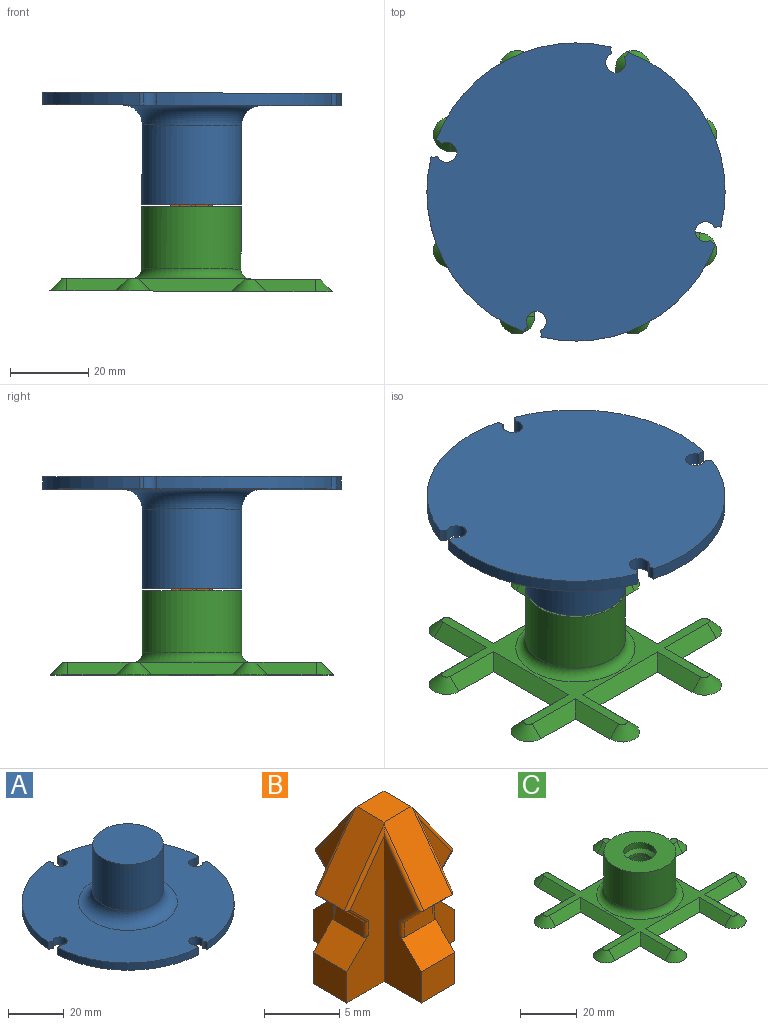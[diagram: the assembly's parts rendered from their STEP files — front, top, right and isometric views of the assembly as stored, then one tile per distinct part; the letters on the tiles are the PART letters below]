
ASSEMBLY  parts=3 mates=1
PART A: 29 faces, bbox 76.1x76.1x28.6 mm
  f0: cylinder r=12.7mm len=25.4mm, axis (0,0,1), area 1621.5mm2, adj f1,f28
  f1: plane 25.4x25.4mm, normal (0,0,1), area 506.7mm2, adj f0
  f2: cylinder r=2.29mm len=3.18mm, axis (0,0,1), area 5.4mm2, adj f3,f25,f26,f27
  f3: cylinder r=38.1mm len=35.75mm, axis (0,0,1), area 175.5mm2, adj f2,f4,f26,f27
  f4: cylinder r=2.29mm len=3.18mm, axis (0,0,1), area 5.4mm2, adj f3,f5,f26,f27
  f5: cylinder r=0.03mm len=3.18mm, axis (0,0,1), area 0.1mm2, adj f4,f6,f26,f27
  f6: cylinder r=2.54mm len=5.08mm, axis (0,0,1), area 39.4mm2, adj f5,f7,f26,f27
  f7: cylinder r=0.03mm len=3.18mm, axis (0,0,1), area 0.1mm2, adj f6,f8,f26,f27
  f8: cylinder r=2.29mm len=3.18mm, axis (0,0,1), area 5.4mm2, adj f7,f9,f26,f27
  f9: cylinder r=38.1mm len=35.75mm, axis (0,0,1), area 175.5mm2, adj f8,f10,f26,f27
  f10: cylinder r=2.29mm len=3.18mm, axis (0,0,1), area 5.4mm2, adj f9,f11,f26,f27
  f11: cylinder r=0.03mm len=3.18mm, axis (0,0,1), area 0.1mm2, adj f10,f12,f26,f27
  f12: cylinder r=2.54mm len=5.08mm, axis (0,0,1), area 39.4mm2, adj f11,f13,f26,f27
  f13: cylinder r=0.03mm len=3.18mm, axis (0,0,1), area 0.1mm2, adj f12,f14,f26,f27
  f14: cylinder r=2.29mm len=3.18mm, axis (0,0,1), area 5.4mm2, adj f13,f15,f26,f27
  f15: cylinder r=38.1mm len=35.75mm, axis (0,0,1), area 175.5mm2, adj f14,f16,f26,f27
  f16: cylinder r=2.29mm len=3.18mm, axis (0,0,1), area 5.4mm2, adj f15,f17,f26,f27
  f17: cylinder r=0.03mm len=3.18mm, axis (0,0,1), area 0.1mm2, adj f16,f18,f26,f27
  f18: cylinder r=2.54mm len=5.08mm, axis (0,0,1), area 39.4mm2, adj f17,f19,f26,f27
  f19: cylinder r=0.03mm len=3.18mm, axis (0,0,1), area 0.1mm2, adj f18,f20,f26,f27
  f20: cylinder r=2.29mm len=3.18mm, axis (0,0,1), area 5.4mm2, adj f19,f21,f26,f27
  f21: cylinder r=38.1mm len=35.75mm, axis (0,0,1), area 175.5mm2, adj f20,f22,f26,f27
  f22: cylinder r=2.29mm len=3.18mm, axis (0,0,1), area 5.4mm2, adj f21,f23,f26,f27
  f23: cylinder r=0.03mm len=3.18mm, axis (0,0,1), area 0.1mm2, adj f22,f24,f26,f27
  f24: cylinder r=2.54mm len=5.08mm, axis (0,0,1), area 39.4mm2, adj f23,f25,f26,f27
  f25: cylinder r=0.03mm len=3.18mm, axis (0,0,1), area 0.1mm2, adj f2,f24,f26,f27
  f26: plane 76.06x76.06mm, normal (0,0,1), area 3464.8mm2, adj f2,f3,f4,f5,f6,f7,f8,f9
  f27: plane 76.06x76.06mm, normal (0,0,-1), area 4458mm2, adj f2,f3,f4,f5,f6,f7,f8,f9
  f28: torus R=17.78mm, axis (0,0,1), area 729.3mm2, adj f0,f26
PART B: 54 faces, bbox 10.2x10.2x12.7 mm
  f0: plane 11.82x3.49mm, normal (1,0,0), area 26.4mm2, adj f5,f14,f15,f29,f45,f46,f47
  f1: plane 11.82x3.49mm, normal (-1,0,0), area 26.4mm2, adj f13,f14,f15,f29,f51,f52,f53
  f2: plane 5.3x3.81mm, normal (-0.81,0,0.58), area 17.4mm2, adj f4,f20,f22,f26,f38,f50
  f3: plane 5.3x3.81mm, normal (0.81,0,0.58), area 17.4mm2, adj f4,f16,f22,f26,f32,f44
  f4: plane 2.54x2.54mm, normal (0,0,1), area 6.5mm2, adj f2,f3,f22,f26
  f5: plane 11.82x3.49mm, normal (0,-1,0), area 26.4mm2, adj f0,f7,f15,f18,f42,f43,f44
  f6: plane 11.82x3.49mm, normal (0,1,0), area 26.4mm2, adj f7,f8,f15,f18,f30,f31,f32
  f7: plane 3.18x2.54mm, normal (1,0,0), area 8.1mm2, adj f5,f6,f15,f18
  f8: plane 11.82x3.49mm, normal (1,0,0), area 26.4mm2, adj f6,f9,f15,f25,f33,f34,f35
  f9: plane 3.18x2.54mm, normal (0,1,0), area 8.1mm2, adj f8,f10,f15,f25
  f10: plane 11.82x3.49mm, normal (-1,0,0), area 26.4mm2, adj f9,f11,f15,f25,f39,f40,f41
  f11: plane 11.82x3.49mm, normal (0,1,0), area 26.4mm2, adj f10,f12,f15,f21,f36,f37,f38
  f12: plane 3.18x2.54mm, normal (-1,0,0), area 8.1mm2, adj f11,f13,f15,f21
  f13: plane 11.82x3.49mm, normal (0,-1,0), area 26.4mm2, adj f1,f12,f15,f21,f48,f49,f50
  f14: plane 3.18x2.54mm, normal (0,-1,0), area 8.1mm2, adj f0,f1,f15,f29
  f15: plane 10.16x10.16mm, normal (0,0,-1), area 54.4mm2, adj f0,f1,f5,f6,f7,f8,f9,f10
  f16: plane 2.67x1.8mm, normal (0.71,0,-0.71), area 6.8mm2, adj f3,f17,f31,f43
  f17: plane 2.67x1.27mm, normal (1,0,0), area 3.4mm2, adj f16,f18,f30,f42
  f18: plane 3.18x2.05mm, normal (0.71,0,0.71), area 8.1mm2, adj f5,f6,f7,f17,f30,f42
  f19: plane 2.67x1.27mm, normal (-1,0,0), area 3.4mm2, adj f20,f21,f36,f48
  f20: plane 2.67x1.8mm, normal (-0.71,0,-0.71), area 6.8mm2, adj f2,f19,f37,f49
  f21: plane 3.18x2.05mm, normal (-0.71,0,0.71), area 8.1mm2, adj f11,f12,f13,f19,f36,f48
  f22: plane 5.3x3.81mm, normal (0,-0.81,0.58), area 17.4mm2, adj f2,f3,f4,f28,f46,f52
  f23: plane 2.67x1.8mm, normal (0,0.71,-0.71), area 6.8mm2, adj f24,f26,f34,f40
  f24: plane 2.67x1.27mm, normal (0,1,0), area 3.4mm2, adj f23,f25,f35,f41
  f25: plane 3.18x2.05mm, normal (0,0.71,0.71), area 8.1mm2, adj f8,f9,f10,f24,f35,f41
  f26: plane 5.3x3.81mm, normal (0,0.81,0.58), area 17.4mm2, adj f2,f3,f4,f23,f33,f39
  f27: plane 2.67x1.27mm, normal (0,-1,0), area 3.4mm2, adj f28,f29,f45,f51
  f28: plane 2.67x1.8mm, normal (0,-0.71,-0.71), area 6.8mm2, adj f22,f27,f47,f53
  f29: plane 3.18x2.05mm, normal (0,-0.71,0.71), area 8.1mm2, adj f0,f1,f14,f27,f45,f51
  f30: cylinder r=0.25mm len=1.38mm, axis (0,0,-1), area 0.5mm2, adj f6,f17,f18,f31
  f31: cylinder r=0.25mm len=2.05mm, axis (-0.71,0,-0.71), area 1mm2, adj f6,f16,f30,f32
  f32: cylinder r=0.25mm len=5.36mm, axis (0.58,0,-0.81), area 2.4mm2, adj f3,f6,f31,f33
  f33: cylinder r=0.25mm len=5.36mm, axis (0,0.58,-0.81), area 2.4mm2, adj f8,f26,f32,f34
  f34: cylinder r=0.25mm len=2.05mm, axis (0,-0.71,-0.71), area 1mm2, adj f8,f23,f33,f35
  f35: cylinder r=0.25mm len=1.38mm, axis (0,0,-1), area 0.5mm2, adj f8,f24,f25,f34
  f36: cylinder r=0.25mm len=1.38mm, axis (0,0,1), area 0.5mm2, adj f11,f19,f21,f37
  f37: cylinder r=0.25mm len=2.05mm, axis (-0.71,0,0.71), area 1mm2, adj f11,f20,f36,f38
  f38: cylinder r=0.25mm len=5.36mm, axis (0.58,0,0.81), area 2.4mm2, adj f2,f11,f37,f39
  f39: cylinder r=0.25mm len=5.36mm, axis (0,-0.58,0.81), area 2.4mm2, adj f10,f26,f38,f40
  f40: cylinder r=0.25mm len=2.05mm, axis (0,0.71,0.71), area 1mm2, adj f10,f23,f39,f41
  f41: cylinder r=0.25mm len=1.38mm, axis (0,0,1), area 0.5mm2, adj f10,f24,f25,f40
  f42: cylinder r=0.25mm len=1.38mm, axis (0,0,1), area 0.5mm2, adj f5,f17,f18,f43
  f43: cylinder r=0.25mm len=2.05mm, axis (0.71,0,0.71), area 1mm2, adj f5,f16,f42,f44
  f44: cylinder r=0.25mm len=5.36mm, axis (-0.58,0,0.81), area 2.4mm2, adj f3,f5,f43,f46
  f45: cylinder r=0.25mm len=1.38mm, axis (0,0,1), area 0.5mm2, adj f0,f27,f29,f47
  f46: cylinder r=0.25mm len=5.36mm, axis (0,0.58,0.81), area 2.4mm2, adj f0,f22,f44,f47
  f47: cylinder r=0.25mm len=2.05mm, axis (0,-0.71,0.71), area 1mm2, adj f0,f28,f45,f46
  f48: cylinder r=0.25mm len=1.38mm, axis (0,0,-1), area 0.5mm2, adj f13,f19,f21,f49
  f49: cylinder r=0.25mm len=2.05mm, axis (0.71,0,-0.71), area 1mm2, adj f13,f20,f48,f50
  f50: cylinder r=0.25mm len=5.36mm, axis (-0.58,0,-0.81), area 2.4mm2, adj f2,f13,f49,f52
  f51: cylinder r=0.25mm len=1.38mm, axis (0,0,-1), area 0.5mm2, adj f1,f27,f29,f53
  f52: cylinder r=0.25mm len=5.36mm, axis (0,-0.58,-0.81), area 2.4mm2, adj f1,f22,f50,f53
  f53: cylinder r=0.25mm len=2.05mm, axis (0,0.71,-0.71), area 1mm2, adj f1,f28,f51,f52
PART C: 38 faces, bbox 72.4x72.4x21.6 mm
  f0: cylinder r=5.71mm len=15.24mm, axis (0,0,-1), area 547.2mm2, adj f3,f8
  f1: cylinder r=5.71mm len=11.43mm, axis (0,0,-1), area 91.2mm2, adj f5,f7
  f2: plane 66.04x66.04mm, normal (0,0,1), area 644mm2, adj f9,f10,f11,f12,f13,f14,f15,f16
  f3: plane 72.39x72.39mm, normal (0,0,-1), area 2517.9mm2, adj f0,f10,f11,f12,f13,f14,f15,f16
  f4: cylinder r=12.7mm len=25.4mm, axis (0,0,-1), area 1266.8mm2, adj f5,f9
  f5: plane 25.4x25.4mm, normal (0,0,1), area 404.1mm2, adj f1,f4
  f6: cylinder r=4.45mm len=8.89mm, axis (0,0,-1), area 35.5mm2, adj f7,f8
  f7: cone r=4.45mm half-angle=45deg, axis (0,0,1), area 57.3mm2, adj f1,f6
  f8: cone r=5.71mm half-angle=45deg, axis (0,0,-1), area 57.3mm2, adj f0,f6
  f9: torus R=15.24mm, axis (0,0,1), area 341.5mm2, adj f2,f4
  f10: plane 27.09x3.18mm, normal (0.71,0,0.71), area 107.4mm2, adj f2,f3,f11,f12
  f11: plane 15.66x3.18mm, normal (0,-0.71,0.71), area 63.2mm2, adj f2,f3,f10,f13
  f12: plane 15.66x3.18mm, normal (0,0.71,0.71), area 63.2mm2, adj f2,f3,f10,f14
  f13: cone r=6.35mm half-angle=45deg, axis (0,0,-1), area 40.3mm2, adj f2,f3,f11,f15
  f14: cone r=1.27mm half-angle=45deg, axis (0,0,-1), area 40.3mm2, adj f2,f3,f12,f16
  f15: plane 15.66x3.18mm, normal (0,0.71,0.71), area 63.2mm2, adj f2,f3,f13,f17
  f16: plane 15.66x3.18mm, normal (0,-0.71,0.71), area 63.2mm2, adj f2,f3,f14,f18
  f17: plane 15.66x3.18mm, normal (0.71,0,0.71), area 63.2mm2, adj f2,f3,f15,f19
  f18: plane 15.66x3.18mm, normal (0.71,0,0.71), area 63.2mm2, adj f2,f3,f16,f20
  f19: cone r=1.27mm half-angle=45deg, axis (0,0,-1), area 40.3mm2, adj f2,f3,f17,f21
  f20: cone r=6.35mm half-angle=45deg, axis (0,0,-1), area 40.3mm2, adj f2,f3,f18,f22
  f21: plane 15.66x3.18mm, normal (-0.71,0,0.71), area 63.2mm2, adj f2,f3,f19,f23
  f22: plane 15.66x3.18mm, normal (-0.71,0,0.71), area 63.2mm2, adj f2,f3,f20,f24
  f23: plane 27.09x3.18mm, normal (0,0.71,0.71), area 107.4mm2, adj f2,f3,f21,f25
  f24: plane 27.09x3.18mm, normal (0,-0.71,0.71), area 107.4mm2, adj f2,f3,f22,f26
  f25: plane 15.66x3.18mm, normal (0.71,0,0.71), area 63.2mm2, adj f2,f3,f23,f27
  f26: plane 15.66x3.18mm, normal (0.71,0,0.71), area 63.2mm2, adj f2,f3,f24,f28
  f27: cone r=6.35mm half-angle=45deg, axis (0,0,-1), area 40.3mm2, adj f2,f3,f25,f29
  f28: cone r=1.27mm half-angle=45deg, axis (0,0,-1), area 40.3mm2, adj f2,f3,f26,f30
  f29: plane 15.66x3.18mm, normal (-0.71,0,0.71), area 63.2mm2, adj f2,f3,f27,f31
  f30: plane 15.66x3.18mm, normal (-0.71,0,0.71), area 63.2mm2, adj f2,f3,f28,f32
  f31: plane 15.66x3.18mm, normal (0,0.71,0.71), area 63.2mm2, adj f2,f3,f29,f33
  f32: plane 15.66x3.18mm, normal (0,-0.71,0.71), area 63.2mm2, adj f2,f3,f30,f34
  f33: cone r=1.27mm half-angle=45deg, axis (0,0,-1), area 40.3mm2, adj f2,f3,f31,f35
  f34: cone r=6.35mm half-angle=45deg, axis (0,0,-1), area 40.3mm2, adj f2,f3,f32,f36
  f35: plane 15.66x3.18mm, normal (0,-0.71,0.71), area 63.2mm2, adj f2,f3,f33,f37
  f36: plane 15.66x3.18mm, normal (0,0.71,0.71), area 63.2mm2, adj f2,f3,f34,f37
  f37: plane 27.09x3.18mm, normal (-0.71,0,0.71), area 107.4mm2, adj f2,f3,f35,f36
PLACE A rot(axis=(0.59,-0.8,0),179.8deg) t=(14.89,5.5,15.28)mm
PLACE B rot(axis=(-0.8,-0.59,0),179.8deg) t=(14.89,5.5,15.28)mm
PLACE C rot(axis=(0,1,0),0.3deg) t=(10.17,18.55,-6.8)mm fixed
MATE fastened B.f15 <-> A.f0  axis (0,0,1) through (14.89,5.5,15.28)mm
